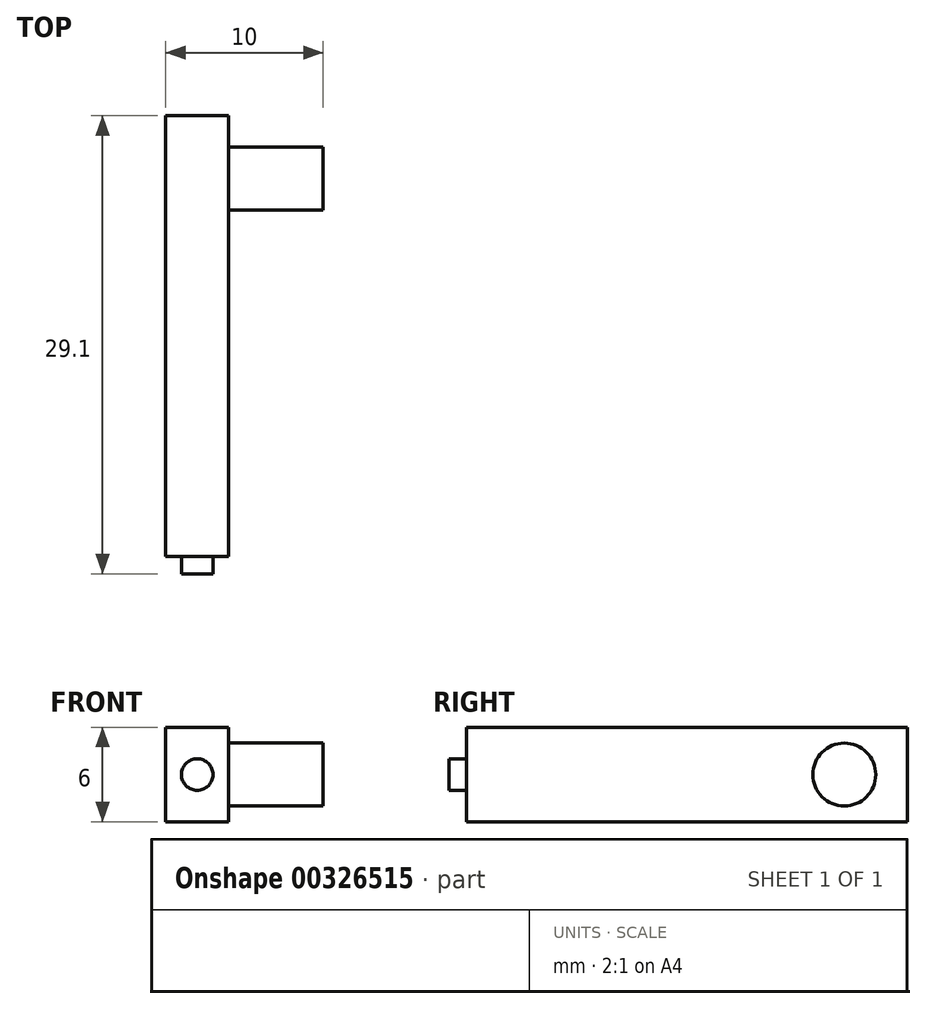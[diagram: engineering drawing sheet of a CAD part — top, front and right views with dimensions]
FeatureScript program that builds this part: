
annotation { "Feature Type Name" : "Feature", "Feature Type Description" : "" }
export const myFeature = defineFeature(function(context is Context, id is Id, definition is map)
    precondition{}
    {
        {
            var Q0;
            Q0=qCreatedBy(makeId("Front.planeOp"),FACE);
            var sketch = newSketch(context, id + "F0", { "sketchPlane" : qUnion([Q0])});
            skLineSegment(sketch, "E0.bottom", {"start": v(-2, 3) * mm, "end": v(2, 3) * mm});
            skLineSegment(sketch, "E0.top", {"start": v(-2, -3) * mm, "end": v(2, -3) * mm});
            skLineSegment(sketch, "E0.left", {"start": v(-2, 3) * mm, "end": v(-2, -3) * mm});
            skLineSegment(sketch, "E0.right", {"start": v(2, 3) * mm, "end": v(2, -3) * mm});
            skPoint(sketch, "E0.middle", {"position": v(0, 0) * mm});
            skSolve(sketch);
        }
        {
            var Q0;
            Q0 = qSketchRegion(id + "F2", true);
            var Q1;
            Q1 = qSketchRegion(id + "F0", true);
            extrude(context, id + "F1", {"entities" : qUnion([Q0, Q1]), "depth" : 28 * mm});
        }
        {
            var Q0;
            Q0=makeQuery(id+"F1.opExtrude","SWEPT_FACE",FACE,{"disambiguationData":[OSD([sQuery(id+"F0.wireOp",EDGE,"E0.right")])]});
            var sketch = newSketch(context, id + "F2", { "sketchPlane" : qUnion([Q0])});
            skCircle(sketch, "E1", {"center": v(-4, 0) * mm, "radius": 2 * mm});
            skSolve(sketch);
        }
        {
            var Q0;
            Q0=makeQuery(id+"F2.imprint","IMPRINT",FACE,{"disambiguationData":[TD([[makeQuery(id+"F2.imprint","IMPRINT",EDGE,{"derivedFrom":sQuery(id+"F2.wireOp",EDGE,"E1")}),1.0]])]});
            extrude(context, id + "F3", {"entities" : qUnion([Q0]), "operationType" : NewBodyOperationType.ADD, "depth" : 6 * mm});
        }
        {
            var Q0;
            Q0=makeQuery(id+"F1.opExtrude","CAP_FACE",FACE,{"disambiguationData":[OSD([sQuery(id+"F0.wireOp",EDGE,"E0.bottom"),sQuery(id+"F0.wireOp",EDGE,"E0.top"),sQuery(id+"F0.wireOp",EDGE,"E0.left"),sQuery(id+"F0.wireOp",EDGE,"E0.right")])],"isStart":false});
            var sketch = newSketch(context, id + "F4", { "sketchPlane" : qUnion([Q0])});
            skCircle(sketch, "E2", {"center": v(0, 0) * mm, "radius": 1 * mm});
            skSolve(sketch);
        }
        {
            var Q0;
            Q0=makeQuery(id+"F4.imprint","IMPRINT",FACE,{"disambiguationData":[TD([[makeQuery(id+"F4.imprint","IMPRINT",EDGE,{"derivedFrom":sQuery(id+"F4.wireOp",EDGE,"E2")}),1.0]])]});
            extrude(context, id + "F5", {"entities" : qUnion([Q0]), "operationType" : NewBodyOperationType.ADD, "depth" : 1.1 * mm});
        }
    });
